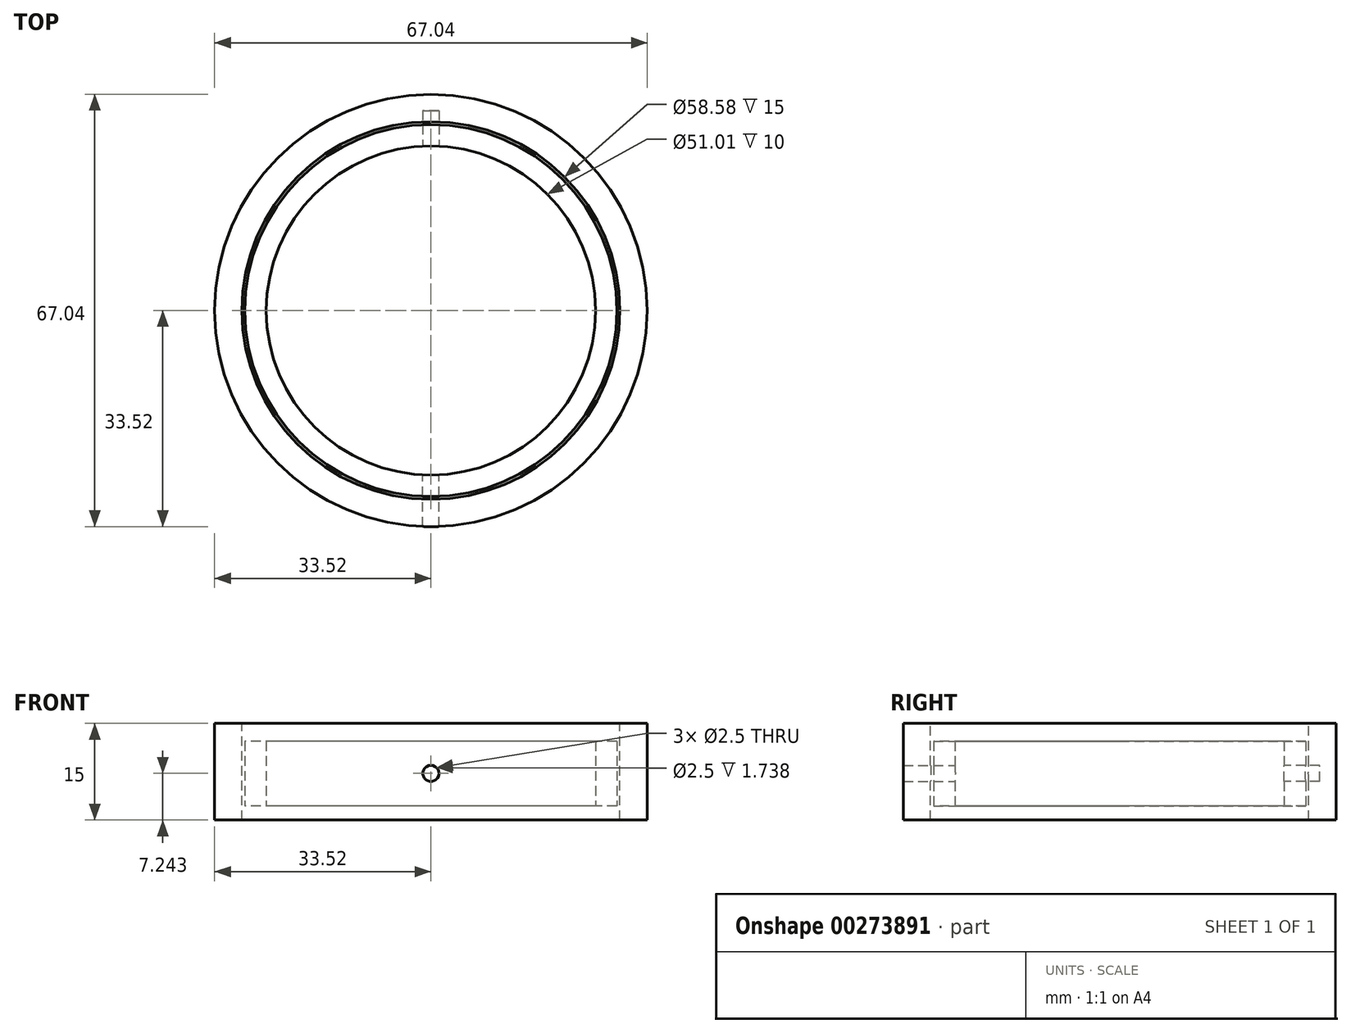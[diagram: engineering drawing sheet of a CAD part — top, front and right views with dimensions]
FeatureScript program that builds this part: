
annotation { "Feature Type Name" : "Feature", "Feature Type Description" : "" }
export const myFeature = defineFeature(function(context is Context, id is Id, definition is map)
    precondition{}
    {
        {
            var Q0;
            Q0=qCreatedBy(makeId("Top.planeOp"),FACE);
            var sketch = newSketch(context, id + "F0", { "sketchPlane" : qUnion([Q0])});
            skCircle(sketch, "E0", {"center": v(0, -0.27) * mm, "radius": 28.67 * mm});
            skSolve(sketch);
        }
        {
            var Q0;
            Q0=qCreatedBy(makeId("Top.planeOp"),FACE);
            cPlane(context, id + "F1", {"entities" : qUnion([Q0]), "cplaneType" : CPlaneType.OFFSET, "offset" : 140 * mm, "width" : 150 * mm, "height" : 150 * mm});
        }
        {
            var Q0;
            Q0=qCreatedBy(id+"F1.planeOp",FACE);
            var sketch = newSketch(context, id + "F2", { "sketchPlane" : qUnion([Q0])});
            skCircle(sketch, "E1", {"center": v(0, 0.28) * mm, "radius": 45.83 * mm});
            skSolve(sketch);
        }
        {
            var Q0;
            Q0=makeQuery(id+"F2.imprint","IMPRINT",FACE,{"disambiguationData":[TD([[makeQuery(id+"F2.imprint","IMPRINT",EDGE,{"derivedFrom":sQuery(id+"F2.wireOp",EDGE,"E1")}),1.0]])]});
            var Q1;
            Q1=makeQuery(id+"F0.imprint","IMPRINT",FACE,{"disambiguationData":[TD([[makeQuery(id+"F0.imprint","IMPRINT",EDGE,{"derivedFrom":sQuery(id+"F0.wireOp",EDGE,"E0")}),1.0]])]});
            loft(context, id + "F3", {"sheetProfilesArray" : [{ "sheetProfileEntities" : qUnion([Q0]) }, { "sheetProfileEntities" : qUnion([Q1]) }]});
        }
        {
            var Q0;
            Q0=makeQuery(id+"F3.opLoft","CAP_FACE",FACE,{"disambiguationData":[OSD([makeQuery(id+"F2.imprint","IMPRINT",FACE,{"disambiguationData":[TD([[makeQuery(id+"F2.imprint","IMPRINT",EDGE,{"derivedFrom":sQuery(id+"F2.wireOp",EDGE,"E1")}),1.0]])]})])],"isStart":true});
            var Q1;
            Q1=makeQuery(id+"F3.opLoft","CAP_FACE",FACE,{"disambiguationData":[OSD([makeQuery(id+"F0.imprint","IMPRINT",FACE,{"disambiguationData":[TD([[makeQuery(id+"F0.imprint","IMPRINT",EDGE,{"derivedFrom":sQuery(id+"F0.wireOp",EDGE,"E0")}),1.0]])]})])],"isStart":true});
            shell(context, id + "F4", {"entities" : qUnion([Q0, Q1]), "thickness" : 2.5 * mm});
        }
        {
            var Q0;
            Q0=makeQuery(id+"F3.opLoft","CAP_FACE",FACE,{"disambiguationData":[OSD([makeQuery(id+"F0.imprint","IMPRINT",FACE,{"disambiguationData":[TD([[makeQuery(id+"F0.imprint","IMPRINT",EDGE,{"derivedFrom":sQuery(id+"F0.wireOp",EDGE,"E0")}),1.0]])]})])],"isStart":true});
            var sketch = newSketch(context, id + "F5", { "sketchPlane" : qUnion([Q0])});
            skCircle(sketch, "E2", {"center": v(0, 0) * mm, "radius": 29.29 * mm});
            skCircle(sketch, "E3", {"center": v(0, 0) * mm, "radius": 33.52 * mm});
            skSolve(sketch);
        }
        {
            var Q0;
            Q0=makeQuery(id+"F5.imprint","IMPRINT",FACE,{"disambiguationData":[TD([[makeQuery(id+"F5.imprint","IMPRINT",EDGE,{"derivedFrom":sQuery(id+"F5.wireOp",EDGE,"E2")}),-1.0]])]});
            extrude(context, id + "F6", {"entities" : qUnion([Q0]), "depth" : 15 * mm});
        }
        {
            var Q0;
            Q0=makeQuery(id+"F3.opLoft","SWEPT_BODY",BODY,{"disambiguationData":[OSD([makeQuery(id+"F0.imprint","IMPRINT",FACE,{"disambiguationData":[TD([[makeQuery(id+"F0.imprint","IMPRINT",EDGE,{"derivedFrom":sQuery(id+"F0.wireOp",EDGE,"E0")}),1.0]])]}),makeQuery(id+"F2.imprint","IMPRINT",FACE,{"disambiguationData":[TD([[makeQuery(id+"F2.imprint","IMPRINT",EDGE,{"derivedFrom":sQuery(id+"F2.wireOp",EDGE,"E1")}),1.0]])]})])]});
            deleteBodies(context, id + "F7", {"entities" : qUnion([Q0])});
        }
        {
            var Q0;
            Q0=qCreatedBy(makeId("Top.planeOp"),FACE);
            cPlane(context, id + "F8", {"entities" : qUnion([Q0]), "cplaneType" : CPlaneType.OFFSET, "offset" : 7.8 * mm, "oppositeDirection" : true, "width" : 150 * mm, "height" : 150 * mm});
        }
        {
            var Q0;
            Q0=qCreatedBy(id+"F8.planeOp",FACE);
            var sketch = newSketch(context, id + "F9", { "sketchPlane" : qUnion([Q0])});
            skCircle(sketch, "E4", {"center": v(0, 0) * mm, "radius": 28.83 * mm});
            skCircle(sketch, "E5", {"center": v(0, 0) * mm, "radius": 25.5 * mm});
            skSolve(sketch);
        }
        {
            var Q0;
            Q0=makeQuery(id+"F9.imprint","IMPRINT",FACE,{"disambiguationData":[TD([[makeQuery(id+"F9.imprint","IMPRINT",EDGE,{"derivedFrom":sQuery(id+"F9.wireOp",EDGE,"E4")}),1.0]])]});
            extrude(context, id + "F10", {"entities" : qUnion([Q0]), "endBound" : BoundingType.SYMMETRIC, "depth" : 10 * mm});
        }
        {
            var Q0;
            Q0=qCreatedBy(makeId("Front.planeOp"),FACE);
            var sketch = newSketch(context, id + "F11", { "sketchPlane" : qUnion([Q0])});
            skCircle(sketch, "E6", {"center": v(0, -7.76) * mm, "radius": 1.25 * mm});
            skSolve(sketch);
        }
        {
            var Q0;
            Q0=makeQuery(id+"F11.imprint","IMPRINT",FACE,{"disambiguationData":[TD([[makeQuery(id+"F11.imprint","IMPRINT",EDGE,{"derivedFrom":sQuery(id+"F11.wireOp",EDGE,"E6")}),1.0]])]});
            extrude(context, id + "F12", {"entities" : qUnion([Q0]), "operationType" : NewBodyOperationType.REMOVE, "endBound" : BoundingType.THROUGH_ALL, "depth" : 25 * mm});
        }
        {
            var Q0;
            Q0=makeQuery(id+"F11.imprint","IMPRINT",FACE,{"disambiguationData":[TD([[makeQuery(id+"F11.imprint","IMPRINT",EDGE,{"derivedFrom":sQuery(id+"F11.wireOp",EDGE,"E6")}),1.0]])]});
            extrude(context, id + "F13", {"entities" : qUnion([Q0]), "operationType" : NewBodyOperationType.REMOVE, "oppositeDirection" : true, "depth" : 31 * mm});
        }
    });
